# Revit family: Lighting_Fixture-Wall-Astro-Serifos
name_source: partatom
category: Lighting Fixtures
revit_build: Autodesk Revit 2014 (Build: 20130308_1515(x64)
units: mm (PartAtom-declared; Revit-internal decimal feet)

## types (1)
- 7375 Serifos
    Apparent Load = 6 VA
    Assembly Code = D5020200
    Casing Material = Astro - Plaster - Natural
    Class = 1
    Color Filter = 16777215
    Description = Wall Light
    Dimmable = No
    Dimming Lamp Color Temperature Shift = <None>
    Energy Efficiency Rating = A++
    Height = 170 mm  [stored 0.557743 ft]
    IP Rating = IP20
    Lamp = LED
    Lamp included = Yes
    Length = 55 mm  [stored 0.180446 ft]
    Light Source Elevation = 1600 mm  [stored 5.24934 ft]
    Light Source From Wall = 30 mm  [stored 0.0984252 ft]
    Luminaire Lamp Efficiency Rating = A++
    Manufacturer = Astro Lighting Ltd, CM20 2DP
    Model = 7375 Serifos
    Mountable on normally flammable surfaces = Yes
    Number of Poles = 1
    Photometric Web File = 7375 SERIFOS 170.ies
    Product Documentation = http://www.astrolighting.co.uk
    Suitable for bathroom zone = Zone 3
    Tilt Angle = 90.00°
    Type Comments = -Astro plaster and ceramic lights can be painted using a good quality emulsion paint. -Includes integral electronic driver
    URL = www.astrolighting.co.uk
    Voltage = 230 V
    Wattage Comments = 2x3w
    Weight = 0.870 kg
    Width = 110 mm  [stored 0.360892 ft]

note: [stored X ft] marks values corroborated as IEEE doubles in the binary element streams (Revit-internal decimal feet)

## geometry (parser evidence)
native form markers: Sweep x6
no freeform markers — native parametric forms only
